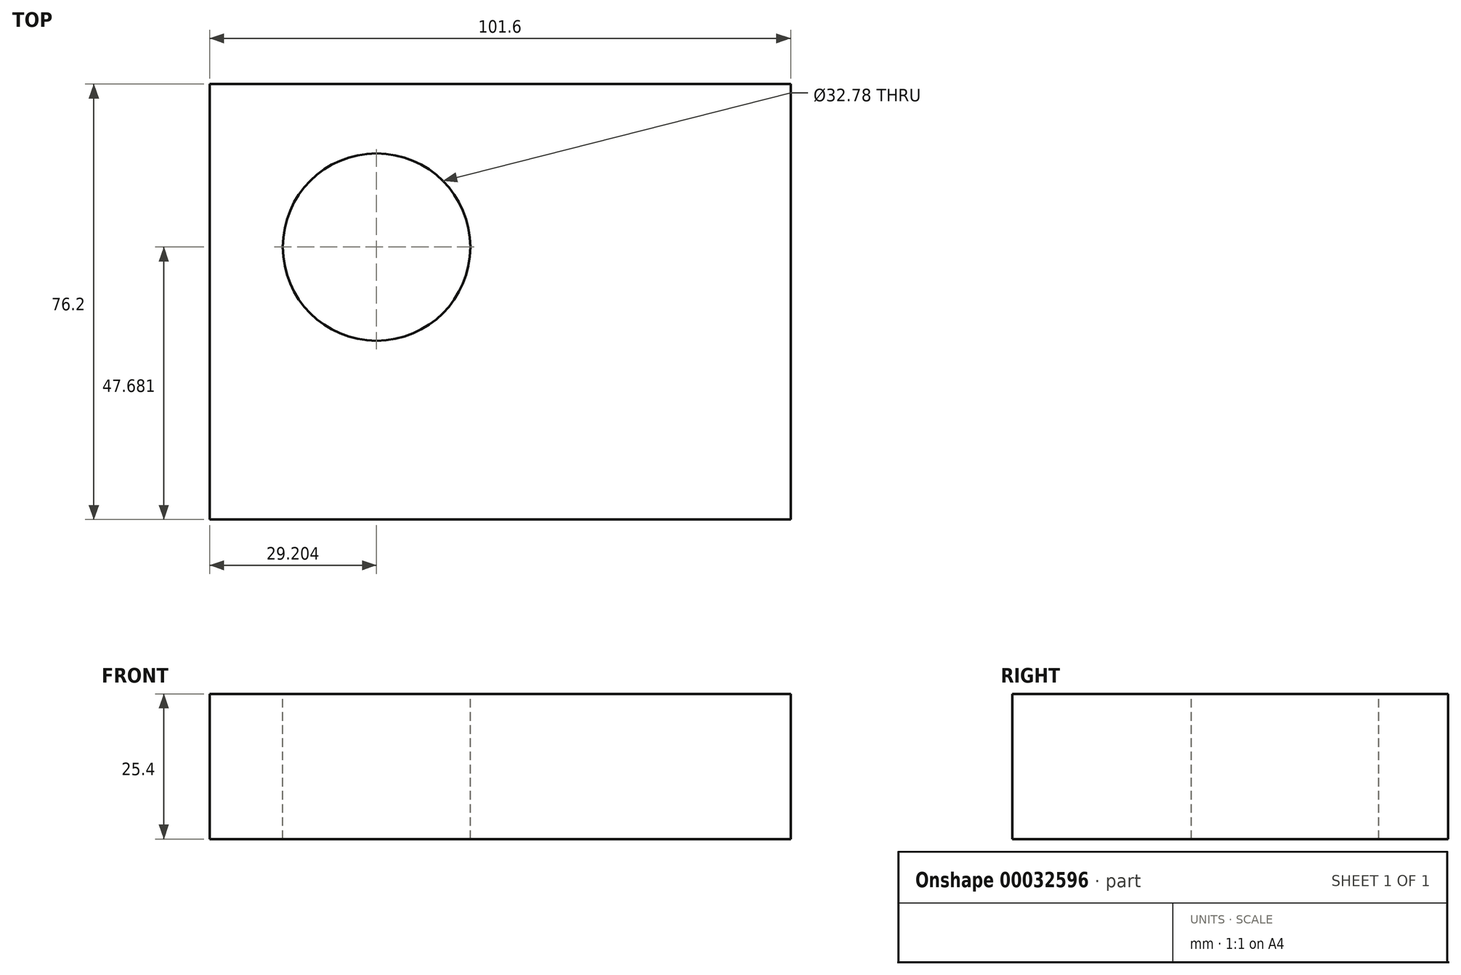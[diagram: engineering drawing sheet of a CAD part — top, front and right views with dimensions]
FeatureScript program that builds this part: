
annotation { "Feature Type Name" : "Feature", "Feature Type Description" : "" }
export const myFeature = defineFeature(function(context is Context, id is Id, definition is map)
    precondition{}
    {
        {
            var Q0;
            Q0=qCreatedBy(makeId("Top.planeOp"),FACE);
            var sketch = newSketch(context, id + "F0", { "sketchPlane" : qUnion([Q0])});
            skLineSegment(sketch, "E0.bottom", {"start": v(-38.74, 40.3) * mm, "end": v(62.86, 40.3) * mm});
            skLineSegment(sketch, "E0.top", {"start": v(-38.74, -35.9) * mm, "end": v(62.86, -35.9) * mm});
            skLineSegment(sketch, "E0.left", {"start": v(-38.74, 40.3) * mm, "end": v(-38.74, -35.9) * mm});
            skLineSegment(sketch, "E0.right", {"start": v(62.86, 40.3) * mm, "end": v(62.86, -35.9) * mm});
            skSolve(sketch);
        }
        {
            var Q0;
            Q0 = qSketchRegion(id + "F0", true);
            extrude(context, id + "F1", {"entities" : qUnion([Q0]), "depth" : 25.4 * mm});
        }
        {
            var Q0;
            Q0=makeQuery(id+"F1.opExtrude","CAP_FACE",FACE,{"disambiguationData":[OSD([sQuery(id+"F0.wireOp",EDGE,"E0.bottom"),sQuery(id+"F0.wireOp",EDGE,"E0.top"),sQuery(id+"F0.wireOp",EDGE,"E0.left"),sQuery(id+"F0.wireOp",EDGE,"E0.right")])],"isStart":false});
            var sketch = newSketch(context, id + "F2", { "sketchPlane" : qUnion([Q0])});
            skCircle(sketch, "E1", {"center": v(-9.54, 11.77) * mm, "radius": 16.39 * mm});
            skSolve(sketch);
        }
        {
            var Q0;
            Q0 = qSketchRegion(id + "F2", true);
            extrude(context, id + "F3", {"entities" : qUnion([Q0]), "operationType" : NewBodyOperationType.REMOVE, "oppositeDirection" : true, "depth" : 25.4 * mm});
        }
    });
